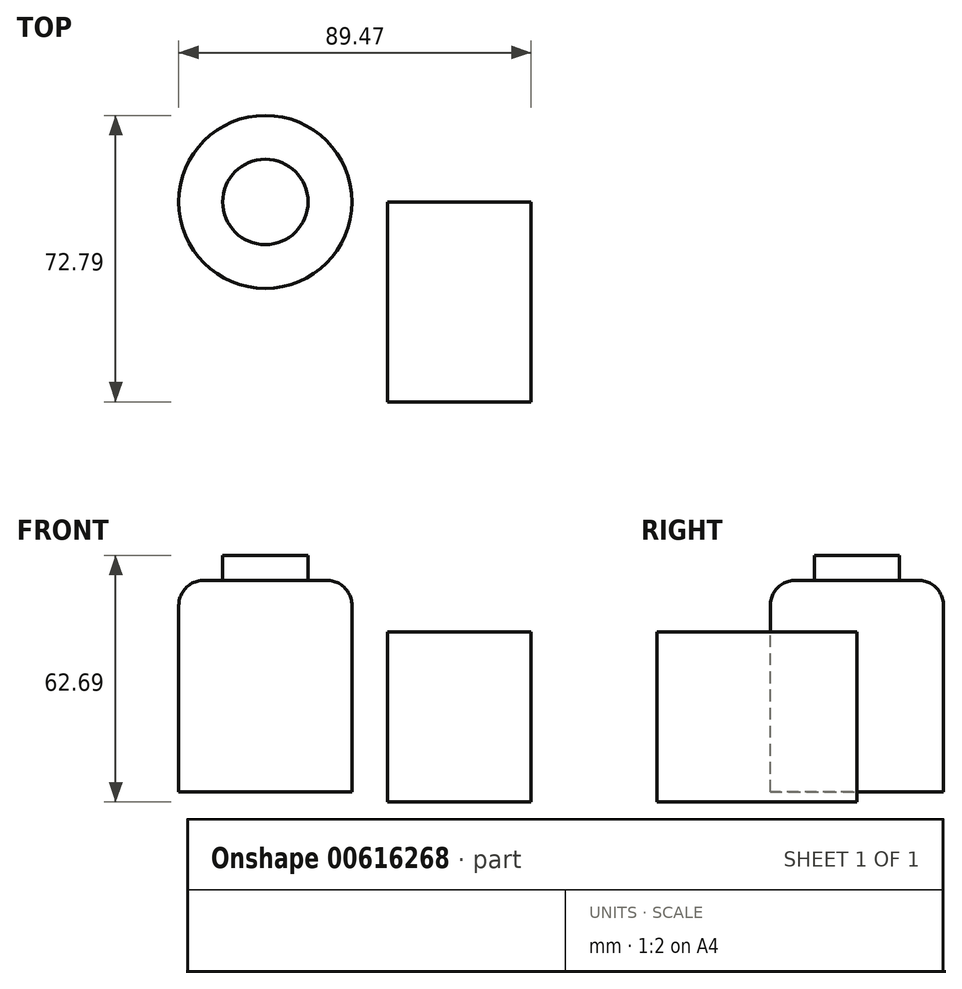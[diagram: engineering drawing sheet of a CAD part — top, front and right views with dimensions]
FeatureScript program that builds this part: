
annotation { "Feature Type Name" : "Feature", "Feature Type Description" : "" }
export const myFeature = defineFeature(function(context is Context, id is Id, definition is map)
    precondition{}
    {
        {
            var Q0;
            Q0=qCreatedBy(makeId("Front.planeOp"),FACE);
            var sketch = newSketch(context, id + "F0", { "sketchPlane" : qUnion([Q0])});
            skLineSegment(sketch, "E0.bottom", {"start": v(0, 0) * mm, "end": v(36.5, 0) * mm});
            skLineSegment(sketch, "E0.top", {"start": v(0, 43.21) * mm, "end": v(36.5, 43.21) * mm});
            skLineSegment(sketch, "E0.left", {"start": v(0, 0) * mm, "end": v(0, 43.21) * mm});
            skLineSegment(sketch, "E0.right", {"start": v(36.5, 0) * mm, "end": v(36.5, 43.21) * mm});
            skSolve(sketch);
        }
        {
            var Q0;
            Q0=makeQuery(id+"F0.imprint","IMPRINT",FACE,{"disambiguationData":[TD([[makeQuery(id+"F0.imprint","IMPRINT",EDGE,{"derivedFrom":sQuery(id+"F0.wireOp",EDGE,"E0.bottom")}),1.0]])]});
            extrude(context, id + "F1", {"entities" : qUnion([Q0]), "depth" : 50.8 * mm, "offsetDistance" : 25.4 * mm});
        }
        {
            var Q0;
            Q0=qCreatedBy(makeId("Front.planeOp"),FACE);
            var sketch = newSketch(context, id + "F2", { "sketchPlane" : qUnion([Q0])});
            skLineSegment(sketch, "E1.bottom", {"start": v(-46.63, 56.34) * mm, "end": v(-31, 56.34) * mm});
            skLineSegment(sketch, "E1.top", {"start": v(-52.98, 2.6) * mm, "end": v(-31, 2.6) * mm});
            skLineSegment(sketch, "E1.left", {"start": v(-52.98, 50) * mm, "end": v(-52.98, 2.6) * mm});
            skLineSegment(sketch, "E1.right", {"start": v(-31, 56.34) * mm, "end": v(-31, 2.6) * mm});
            skPoint(sketch, "E1.middle", {"position": v(-41.99, 29.47) * mm});
            skPoint(sketch, "E2.visualSharp", {"position": v(-52.98, 56.34) * mm});
            skArc(sketch, "E2.filletArc", {"start": v(-46.63, 56.34) * mm, "mid": v(-51.12, 54.48) * mm, "end": v(-52.98, 50) * mm});
            skSolve(sketch);
        }
        {
            var Q0;
            Q0=makeQuery(id+"F2.imprint","IMPRINT",FACE,{"disambiguationData":[TD([[makeQuery(id+"F2.imprint","IMPRINT",EDGE,{"derivedFrom":sQuery(id+"F2.wireOp",EDGE,"E1.bottom")}),-1.0]])]});
            var Q1;
            Q1=sQuery(id+"F2.wireOp",EDGE,"E1.right");
            revolve(context, id + "F3", {"entities" : qUnion([Q0]), "axis" : qUnion([Q1]), "revolveType" : RevolveType.FULL});
        }
        {
            var Q0;
            Q0=makeQuery(id+"F3.opRevolve","SWEPT_FACE",FACE,{"disambiguationData":[OSD([sQuery(id+"F2.wireOp",EDGE,"E1.bottom")])]});
            var sketch = newSketch(context, id + "F4", { "sketchPlane" : qUnion([Q0])});
            skCircle(sketch, "E3", {"center": v(-31, 0) * mm, "radius": 10.85 * mm});
            skSolve(sketch);
        }
        {
            var Q0;
            Q0 = qSketchRegion(id + "F4", true);
            extrude(context, id + "F5", {"entities" : qUnion([Q0]), "operationType" : NewBodyOperationType.ADD, "depth" : 6.35 * mm, "offsetDistance" : 25.4 * mm});
        }
    });
